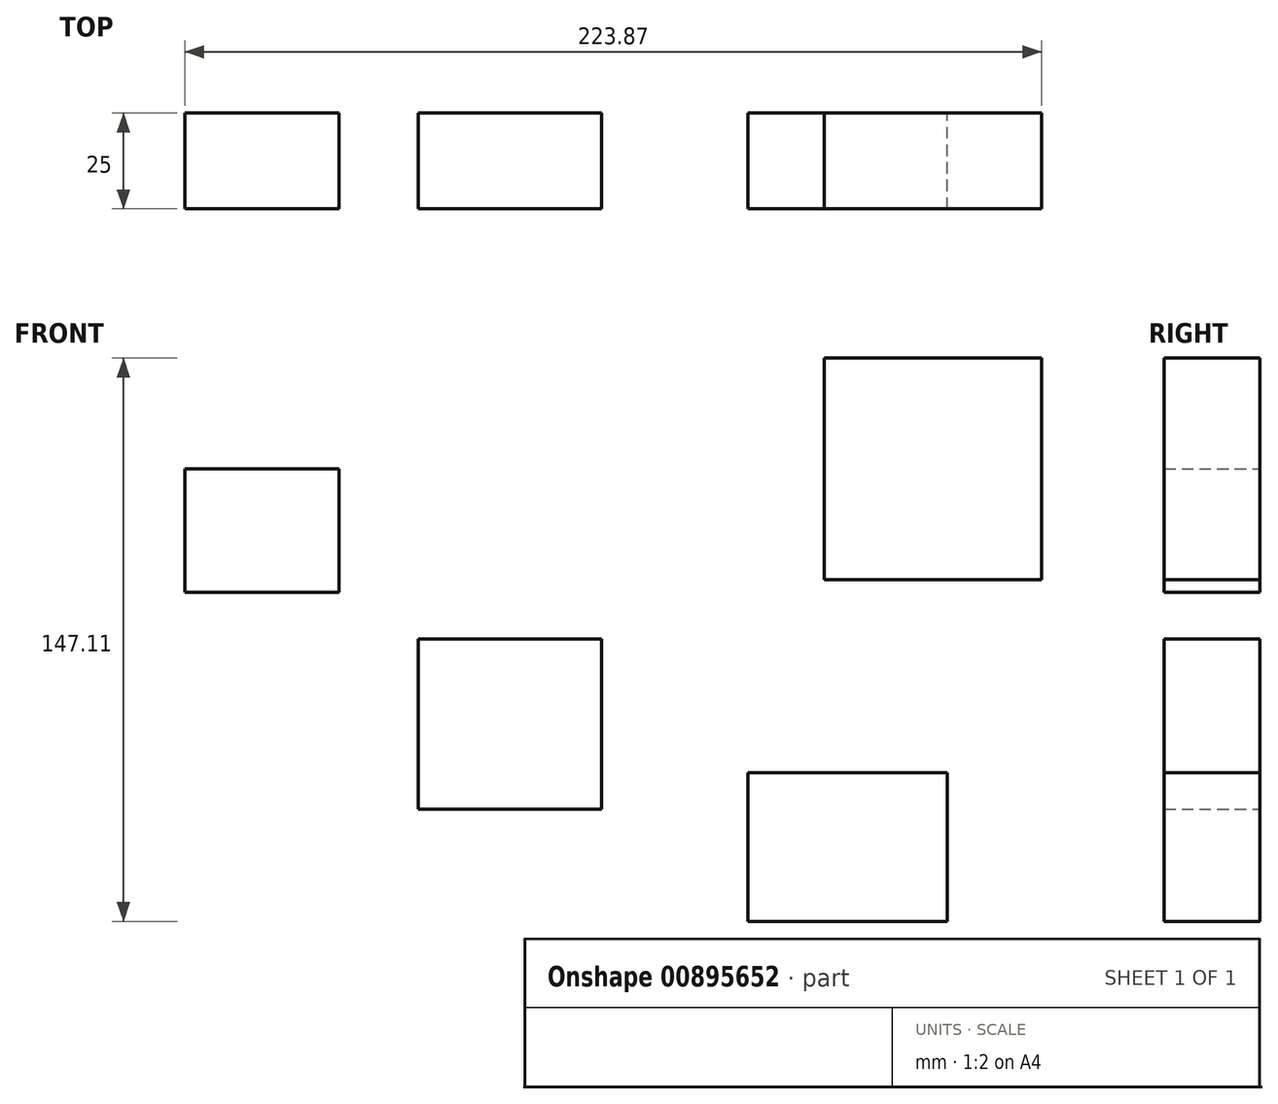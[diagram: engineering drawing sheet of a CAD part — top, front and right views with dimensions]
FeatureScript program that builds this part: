
annotation { "Feature Type Name" : "Feature", "Feature Type Description" : "" }
export const myFeature = defineFeature(function(context is Context, id is Id, definition is map)
    precondition{}
    {
        {
            var Q0;
            Q0=qCreatedBy(makeId("Front.planeOp"),FACE);
            var sketch = newSketch(context, id + "F0", { "sketchPlane" : qUnion([Q0])});
            skLineSegment(sketch, "E0.bottom", {"start": v(-131.93, 44.4) * mm, "end": v(-91.58, 44.4) * mm});
            skLineSegment(sketch, "E0.top", {"start": v(-131.93, 12.12) * mm, "end": v(-91.58, 12.12) * mm});
            skLineSegment(sketch, "E0.left", {"start": v(-131.93, 44.4) * mm, "end": v(-131.93, 12.12) * mm});
            skLineSegment(sketch, "E0.right", {"start": v(-91.58, 44.4) * mm, "end": v(-91.58, 12.12) * mm});
            skLineSegment(sketch, "E1.bottom", {"start": v(-70.88, 0) * mm, "end": v(-23.03, 0) * mm});
            skLineSegment(sketch, "E1.top", {"start": v(-70.88, -44.5) * mm, "end": v(-23.03, -44.5) * mm});
            skLineSegment(sketch, "E1.left", {"start": v(-70.88, 0) * mm, "end": v(-70.88, -44.5) * mm});
            skLineSegment(sketch, "E1.right", {"start": v(-23.03, 0) * mm, "end": v(-23.03, -44.5) * mm});
            skLineSegment(sketch, "E2.bottom", {"start": v(15.17, -34.9) * mm, "end": v(67.3, -34.9) * mm});
            skLineSegment(sketch, "E2.top", {"start": v(15.17, -73.76) * mm, "end": v(67.3, -73.76) * mm});
            skLineSegment(sketch, "E2.left", {"start": v(15.17, -34.9) * mm, "end": v(15.17, -73.76) * mm});
            skLineSegment(sketch, "E2.right", {"start": v(67.3, -34.9) * mm, "end": v(67.3, -73.76) * mm});
            skLineSegment(sketch, "E3.bottom", {"start": v(35.17, 73.35) * mm, "end": v(91.94, 73.35) * mm});
            skLineSegment(sketch, "E3.top", {"start": v(35.17, 15.47) * mm, "end": v(91.94, 15.47) * mm});
            skLineSegment(sketch, "E3.left", {"start": v(35.17, 73.35) * mm, "end": v(35.17, 15.47) * mm});
            skLineSegment(sketch, "E3.right", {"start": v(91.94, 73.35) * mm, "end": v(91.94, 15.47) * mm});
            skSolve(sketch);
        }
        {
            var Q0;
            Q0 = qSketchRegion(id + "F0", true);
            extrude(context, id + "F1", {"entities" : qUnion([Q0]), "depth" : 25 * mm, "offsetDistance" : 25 * mm});
        }
    });
